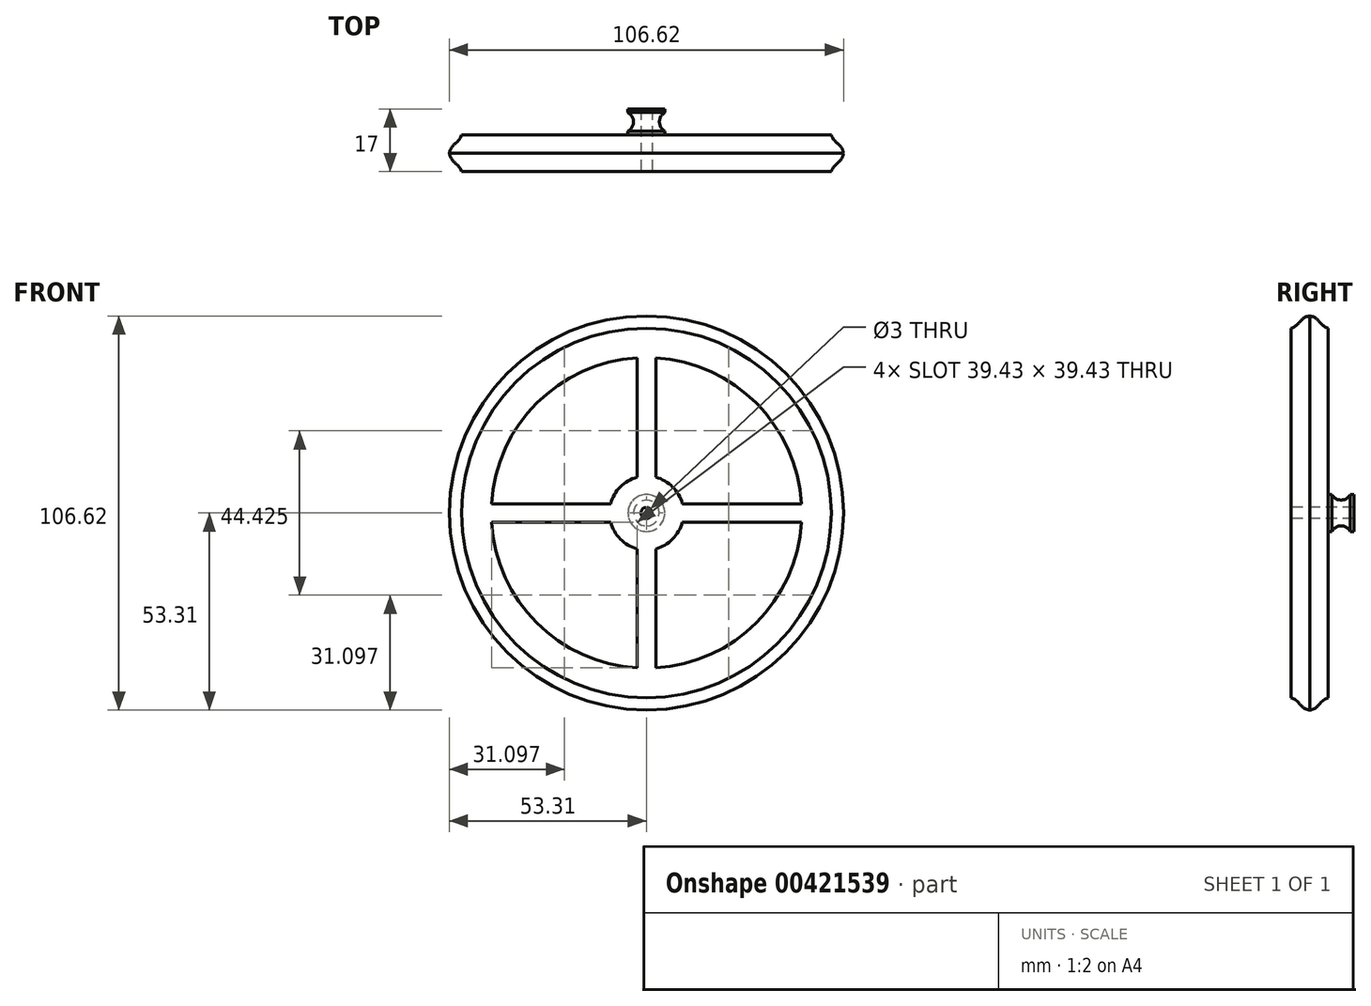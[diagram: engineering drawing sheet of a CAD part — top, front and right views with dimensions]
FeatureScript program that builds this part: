
annotation { "Feature Type Name" : "Feature", "Feature Type Description" : "" }
export const myFeature = defineFeature(function(context is Context, id is Id, definition is map)
    precondition{}
    {
        {
            var Q0;
            Q0=qCreatedBy(makeId("Front.planeOp"),FACE);
            var sketch = newSketch(context, id + "F0", { "sketchPlane" : qUnion([Q0])});
            skCircle(sketch, "E0", {"center": v(0, 0) * mm, "radius": 50 * mm});
            skSolve(sketch);
        }
        {
            var Q0;
            Q0=qSketchRegion(id+"F0",true);
            extrude(context, id + "F1", {"entities" : qUnion([Q0]), "depth" : 10 * mm});
        }
        {
            var Q0;
            Q0=qCreatedBy(makeId("Right.planeOp"),FACE);
            var sketch = newSketch(context, id + "F2", { "sketchPlane" : qUnion([Q0])});
            skLineSegment(sketch, "E1", {"start": v(0, 0) * mm, "end": v(-41.88, 0) * mm});
            skSolve(sketch);
        }
        {
            var Q0;
            Q0=qCreatedBy(makeId("Right.planeOp"),FACE);
            var sketch = newSketch(context, id + "F3", { "sketchPlane" : qUnion([Q0])});
            skLineSegment(sketch, "E2", {"start": v(0, 50) * mm, "end": v(-10, 50) * mm, "construction": true});
            skPoint(sketch, "E3.1.internal.snap0", {"position": v(-5, 50) * mm});
            skFitSpline(sketch, "E3", {"points": [v(0, 50) * mm, v(-5, 53.3) * mm], "startDerivative": vector(-7.76, 2.57) * mm, "endDerivative": vector(-8.1, 1.22) * mm});
            skLineSegment(sketch, "E4", {"start": v(-5, 53.3) * mm, "end": v(-5, 50) * mm, "construction": true});
            skFitSpline(sketch, "E5.MirrorCS", {"points": [v(-10, 50) * mm, v(-5, 53.3) * mm], "startDerivative": vector(7.76, 2.57) * mm, "endDerivative": vector(8.1, 1.22) * mm});
            skLineSegment(sketch, "E6", {"start": v(0, 50) * mm, "end": v(-10, 50) * mm});
            skSolve(sketch);
        }
        {
            var Q0;
            Q0=qSketchRegion(id+"F3",true);
            var Q1;
            Q1=sQuery(id+"F2.wireOp",EDGE,"E1");
            revolve(context, id + "F4", {"operationType" : NewBodyOperationType.ADD, "entities" : qUnion([Q0]), "axis" : qUnion([Q1]), "revolveType" : RevolveType.FULL});
        }
        {
            var Q0;
            Q0=makeQuery(id+"F1.opExtrude","CAP_FACE",FACE,{"disambiguationData":[OSD([sQuery(id+"F0.wireOp",EDGE,"E0")])],"isStart":false});
            var sketch = newSketch(context, id + "F5", { "sketchPlane" : qUnion([Q0])});
            skCircle(sketch, "E7", {"center": v(0, 0) * mm, "radius": 1.5 * mm});
            skSolve(sketch);
        }
        {
            var Q0;
            Q0=makeQuery(id+"F1.opExtrude","CAP_FACE",FACE,{"disambiguationData":[OSD([sQuery(id+"F0.wireOp",EDGE,"E0")])],"isStart":true});
            var sketch = newSketch(context, id + "F6", { "sketchPlane" : qUnion([Q0])});
            skCircle(sketch, "E8", {"center": v(0, 0) * mm, "radius": 5 * mm});
            skSolve(sketch);
        }
        {
            var Q0;
            Q0 = qSketchRegion(id + "F6", true);
            extrude(context, id + "F7", {"entities" : qUnion([Q0]), "operationType" : NewBodyOperationType.ADD, "depth" : 7 * mm});
        }
        {
            var Q0;
            Q0=qSketchRegion(id+"F5",true);
            extrude(context, id + "F8", {"entities" : qUnion([Q0]), "operationType" : NewBodyOperationType.REMOVE, "endBound" : BoundingType.THROUGH_ALL, "oppositeDirection" : true, "depth" : 25 * mm});
        }
        {
            var Q0;
            Q0=qCreatedBy(makeId("Right.planeOp"),FACE);
            var sketch = newSketch(context, id + "F9", { "sketchPlane" : qUnion([Q0])});
            skLineSegment(sketch, "E9.bottom", {"start": v(7, 5) * mm, "end": v(0, 5) * mm, "construction": true});
            skLineSegment(sketch, "E9.top", {"start": v(7, -5) * mm, "end": v(0, -5) * mm, "construction": true});
            skLineSegment(sketch, "E9.left", {"start": v(7, 5) * mm, "end": v(7, -5) * mm, "construction": true});
            skLineSegment(sketch, "E9.right", {"start": v(0, 5) * mm, "end": v(0, -5) * mm, "construction": true});
            skPoint(sketch, "E9.middle", {"position": v(3.5, 0) * mm});
            skArc(sketch, "E10", {"start": v(1, 5) * mm, "mid": v(3.5, 3.5) * mm, "end": v(6, 5) * mm});
            skLineSegment(sketch, "E11", {"start": v(1, 5) * mm, "end": v(6, 5) * mm});
            skSolve(sketch);
        }
        {
            var Q0;
            Q0=qCreatedBy(makeId("Right.planeOp"),FACE);
            var sketch = newSketch(context, id + "F10", { "sketchPlane" : qUnion([Q0])});
            skLineSegment(sketch, "E12", {"start": v(-10.54, 0) * mm, "end": v(17, 0) * mm});
            skSolve(sketch);
        }
        {
            var Q0;
            Q0 = qSketchRegion(id + "F9", true);
            var Q1;
            Q1=sQuery(id+"F10.wireOp",EDGE,"E12");
            revolve(context, id + "F11", {"operationType" : NewBodyOperationType.REMOVE, "entities" : qUnion([Q0]), "axis" : qUnion([Q1]), "revolveType" : RevolveType.FULL});
        }
        {
            var Q0;
            Q0=makeQuery(id+"F1.opExtrude","CAP_FACE",FACE,{"disambiguationData":[OSD([sQuery(id+"F0.wireOp",EDGE,"E0")])],"isStart":true});
            var sketch = newSketch(context, id + "F12", { "sketchPlane" : qUnion([Q0])});
            skArc(sketch, "E13", {"start": v(41.93, 2.5) * mm, "mid": v(29.7, 29.7) * mm, "end": v(2.5, 41.93) * mm});
            skArc(sketch, "E14", {"start": v(9.68, 2.5) * mm, "mid": v(7.07, 7.07) * mm, "end": v(2.5, 9.68) * mm});
            skLineSegment(sketch, "E15", {"start": v(9.68, 2.5) * mm, "end": v(41.93, 2.5) * mm});
            skLineSegment(sketch, "E16", {"start": v(2.5, 41.93) * mm, "end": v(2.5, 9.68) * mm});
            skArc(sketch, "E17.MirrorCS", {"start": v(41.93, -2.5) * mm, "mid": v(29.7, -29.7) * mm, "end": v(2.5, -41.93) * mm});
            skLineSegment(sketch, "E18.MirrorCS", {"start": v(9.68, -2.5) * mm, "end": v(41.93, -2.5) * mm});
            skArc(sketch, "E19.MirrorCS", {"start": v(9.68, -2.5) * mm, "mid": v(7.07, -7.07) * mm, "end": v(2.5, -9.68) * mm});
            skLineSegment(sketch, "E20.MirrorCS", {"start": v(2.5, -41.93) * mm, "end": v(2.5, -9.68) * mm});
            skLineSegment(sketch, "E21.MirrorCS", {"start": v(-2.5, 41.93) * mm, "end": v(-2.5, 9.68) * mm});
            skArc(sketch, "E22.MirrorCS", {"start": v(-9.68, 2.5) * mm, "mid": v(-7.07, 7.07) * mm, "end": v(-2.5, 9.68) * mm});
            skLineSegment(sketch, "E23.MirrorCS", {"start": v(-9.68, -2.5) * mm, "end": v(-41.93, -2.5) * mm});
            skLineSegment(sketch, "E24.MirrorCS", {"start": v(-9.68, 2.5) * mm, "end": v(-41.93, 2.5) * mm});
            skArc(sketch, "E25.MirrorCS", {"start": v(-41.93, 2.5) * mm, "mid": v(-29.7, 29.7) * mm, "end": v(-2.5, 41.93) * mm});
            skArc(sketch, "E26.MirrorCS", {"start": v(-41.93, -2.5) * mm, "mid": v(-29.7, -29.7) * mm, "end": v(-2.5, -41.93) * mm});
            skLineSegment(sketch, "E27.MirrorCS", {"start": v(-2.5, -41.93) * mm, "end": v(-2.5, -9.68) * mm});
            skArc(sketch, "E28.MirrorCS", {"start": v(-9.68, -2.5) * mm, "mid": v(-7.07, -7.07) * mm, "end": v(-2.5, -9.68) * mm});
            skSolve(sketch);
        }
        {
            var Q0;
            Q0 = qSketchRegion(id + "F12", true);
            extrude(context, id + "F13", {"entities" : qUnion([Q0]), "operationType" : NewBodyOperationType.REMOVE, "endBound" : BoundingType.THROUGH_ALL, "oppositeDirection" : true, "depth" : 25 * mm});
        }
    });
